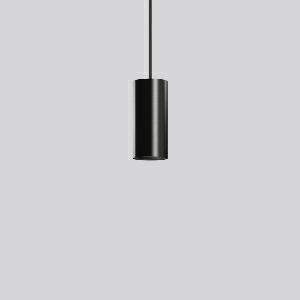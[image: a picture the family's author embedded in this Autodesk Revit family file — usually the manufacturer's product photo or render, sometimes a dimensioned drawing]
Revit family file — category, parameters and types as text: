
# Revit family: deecos_p_mini_911513_003_9505
name_source: partatom
category: Lighting Fixtures
units: mm (PartAtom-declared; Revit-internal decimal feet)

## family parameters
Cut with Voids When Loaded = No
Host = Face
Light Source = No
Part Type = Normal
Room Calculation Point = No
Round Connector Dimension = Use Diameter
Shared = No

## types (1)
- DEECOS P mini (1 x LED Modul 930, 2500 lm, 3000)
    Apparent Load = 20 VA
    Approval mark = CE
    CIE Flux Codes = 100 100 100 100 100
    Color Rendering = 90
    Color Temperature = 3000
    Default Elevation = 1800 mm
    Description = Series: DEECOS P mini
Cylindrical pendant luminaire. Housing: die-cast aluminium, powder-coated. Canopy made of powder-coated sheet steel with magnetic attachment. Optical assembly with reflector made of MIRO-Silver with 98% total light reflection for outstanding efficiency - can be changed without tools. Best colour rendering index Ra>90. Transparent pendant cable 5 m, can be shortened, with integrated steel cable. High quality converter without flickering and stroboscopic effect. The following accessories can be mounted without use of tools: interchangeable lenses, honeycomb louvre, clear and frosted diffusers, white interchangeable plastic ring. Decorative recessed suspension set available as accessory.Suitable for accessory Deecos P Tube cylinder extensions 0.5 m, 0.75 m or 1 m. 
Colour: deep black, matt (RAL 9005)
Diameter: 87 mm
Height: 195 mm
Suspension length: 5000 mm
Lamp: LED
Socket: without socket
Colour temperature: 3000K
Colour rendering index (CRI): 92
System power: 20 W
Rated luminous flux: 2500 lm
Luminous efficiency: 125 lm/W
Control gear: Regulated power supply
Protection class: I
Type of protection: IP 20
    Height = 195 mm
    Lamp = 1 x LED Modul 930
    Lamp Light Flux = 2500 lm
    Lamp count = 1
    Length = 87 mm
    Lifetime = 50000 h
    Luminous efficacy = 125 lm/W
    Manufacturer = RZB
    ModVariant = No
    Model = 911513.003
    Mounting Place = Ceiling
    Mounting Type = Pendant
    Number of Poles = 1
    OnlyDefault = Yes
    Power Factor = 1
    Product Name = DEECOS P mini
    Product group = Pendant luminaires
    ProductGroupID = 902
    Protection Class = Protection class I
    Protection Degree = IP 20
    RLX_Detail_Level = 1
    RLX_Emergency_Light_Flux = 0 lm
    RLX_Emergency_Type = 0
    RLX_Emergency_Type_DB = No
    RlxData = <blob elided: 57173 chars, md5=3019be8c>
    Socket = socket
    Standby Power = 0 W
    System Light Flux = 2500 lm
    System Power = 20 W
    Type Comments = Product without accessories
    Type Image = 911476.003.jpg
    URL = http://relux.com
    VarID = ---
    Voltage = 230 V
    Voltage Range = 220-240 V
    Weight = 0.00 kg
    Width = 0 mm  [stored 0 ft]

note: [stored X ft] marks values corroborated as IEEE doubles in the binary element streams (Revit-internal decimal feet)

## geometry (parser evidence)
native form markers: Blend x4, Sweep x14
no freeform markers — native parametric forms only
